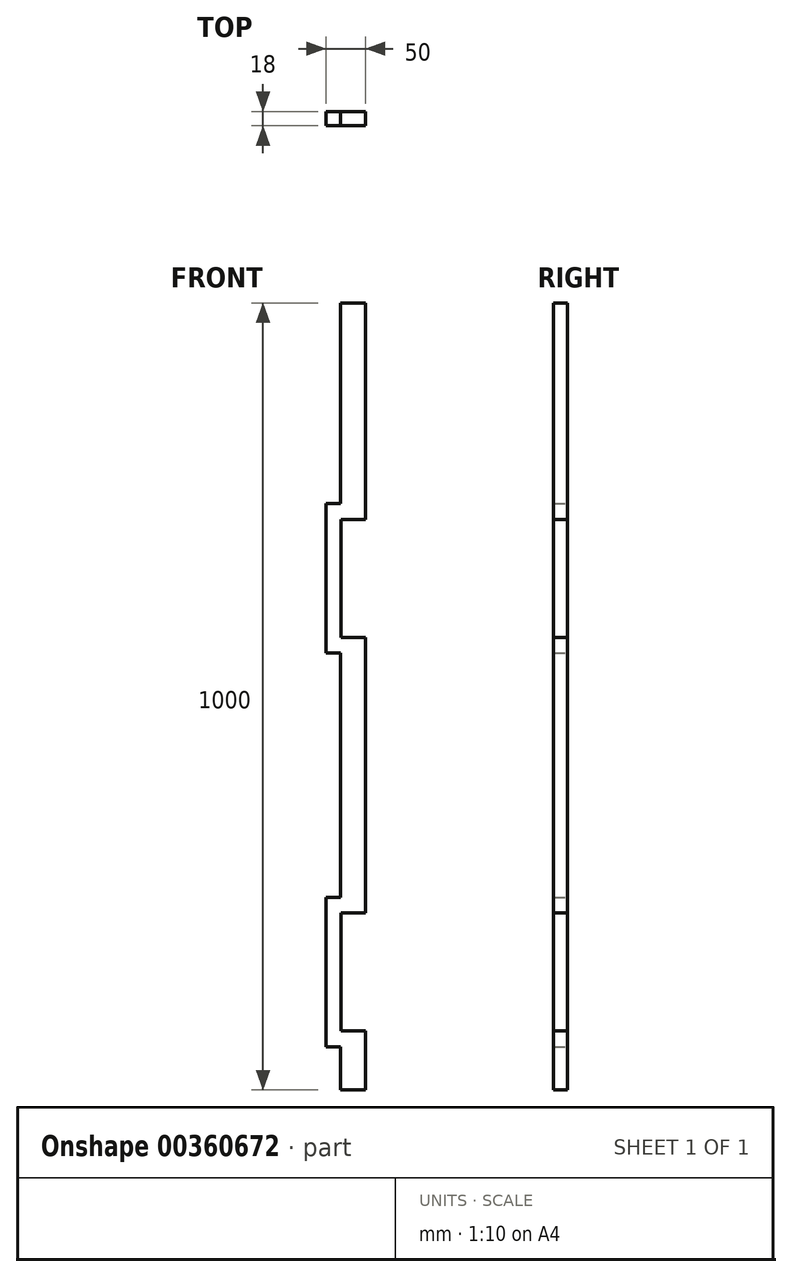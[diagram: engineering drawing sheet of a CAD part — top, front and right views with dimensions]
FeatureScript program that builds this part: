
annotation { "Feature Type Name" : "Feature", "Feature Type Description" : "" }
export const myFeature = defineFeature(function(context is Context, id is Id, definition is map)
    precondition{}
    {
        {
            var Q0;
            Q0=qCreatedBy(makeId("Front.planeOp"),FACE);
            var sketch = newSketch(context, id + "F0", { "sketchPlane" : qUnion([Q0])});
            skLineSegment(sketch, "E0.bottom", {"start": v(0, 0) * mm, "end": v(32, 0) * mm});
            skLineSegment(sketch, "E0.top", {"start": v(0, 1000) * mm, "end": v(32, 1000) * mm});
            skLineSegment(sketch, "E0.left", {"start": v(0, 0) * mm, "end": v(0, 54.64) * mm});
            skLineSegment(sketch, "E0.right", {"start": v(32, 0) * mm, "end": v(32, 75) * mm});
            skLineSegment(sketch, "E1.bottom", {"start": v(32, 725) * mm, "end": v(1, 725) * mm});
            skLineSegment(sketch, "E1.top", {"start": v(32, 575) * mm, "end": v(1, 575) * mm});
            skLineSegment(sketch, "E1.right", {"start": v(1, 725) * mm, "end": v(1, 575) * mm});
            skLineSegment(sketch, "E2.bottom", {"start": v(32, 225) * mm, "end": v(1, 225) * mm});
            skLineSegment(sketch, "E2.top", {"start": v(32, 75) * mm, "end": v(1, 75) * mm});
            skLineSegment(sketch, "E2.right", {"start": v(1, 225) * mm, "end": v(1, 75) * mm});
            skLineSegment(sketch, "E3.trimOffspring", {"start": v(32, 725) * mm, "end": v(32, 1000) * mm});
            skLineSegment(sketch, "E4.trimOffspring", {"start": v(32, 225) * mm, "end": v(32, 575) * mm});
            skLineSegment(sketch, "E5.bottom", {"start": v(-18, 745) * mm, "end": v(0, 745) * mm});
            skLineSegment(sketch, "E5.top", {"start": v(-18, 555) * mm, "end": v(0, 555) * mm});
            skLineSegment(sketch, "E5.left", {"start": v(-18, 745) * mm, "end": v(-18, 555) * mm});
            skLineSegment(sketch, "E6.trimOffspring", {"start": v(0, 745) * mm, "end": v(0, 1000) * mm});
            skLineSegment(sketch, "E7", {"start": v(0, 244.64) * mm, "end": v(-18, 244.64) * mm});
            skLineSegment(sketch, "E8", {"start": v(-18, 244.64) * mm, "end": v(-18, 54.64) * mm});
            skLineSegment(sketch, "E9", {"start": v(-18, 54.64) * mm, "end": v(0, 54.64) * mm});
            skLineSegment(sketch, "E10.trimOffspring", {"start": v(0, 244.64) * mm, "end": v(0, 555) * mm});
            skSolve(sketch);
        }
        {
            var Q0;
            Q0=makeQuery(id+"F0.imprint","IMPRINT",FACE,{"disambiguationData":[TD([[makeQuery(id+"F0.imprint","IMPRINT",EDGE,{"derivedFrom":sQuery(id+"F0.wireOp",EDGE,"E0.bottom")}),1.0]])]});
            extrude(context, id + "F1", {"entities" : qUnion([Q0]), "depth" : 18 * mm});
        }
    });
